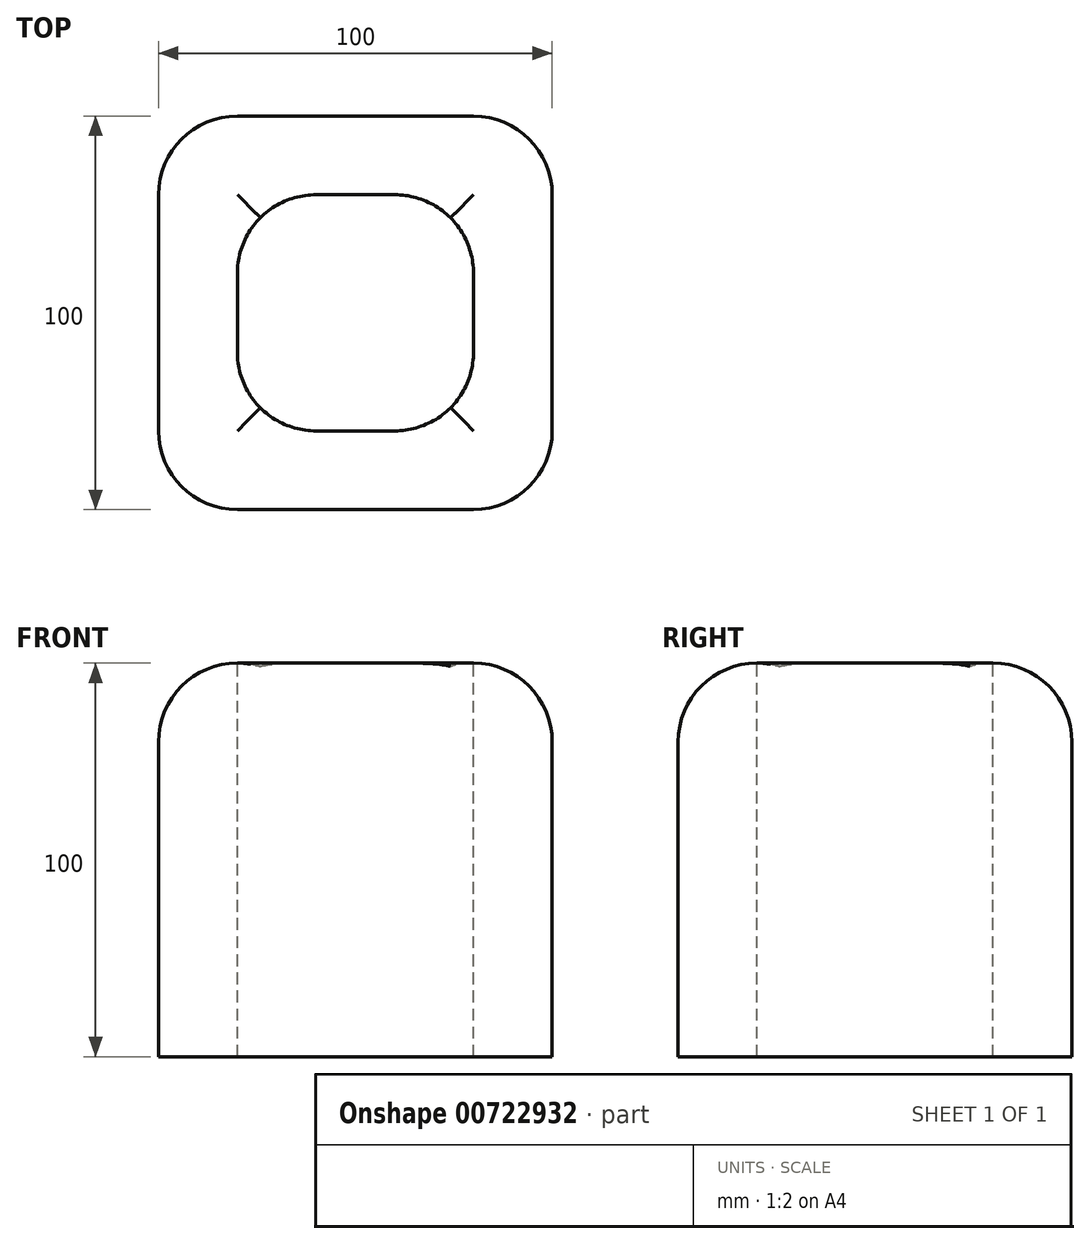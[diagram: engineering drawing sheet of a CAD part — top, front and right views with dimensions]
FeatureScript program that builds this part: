
annotation { "Feature Type Name" : "Feature", "Feature Type Description" : "" }
export const myFeature = defineFeature(function(context is Context, id is Id, definition is map)
    precondition{}
    {
        {
            var Q0;
            Q0=qCreatedBy(makeId("Top.planeOp"),FACE);
            var sketch = newSketch(context, id + "F0", { "sketchPlane" : qUnion([Q0])});
            skLineSegment(sketch, "E0.bottom", {"start": v(-50, 50) * mm, "end": v(50, 50) * mm});
            skLineSegment(sketch, "E0.top", {"start": v(-50, -50) * mm, "end": v(50, -50) * mm});
            skLineSegment(sketch, "E0.left", {"start": v(-50, 50) * mm, "end": v(-50, -50) * mm});
            skLineSegment(sketch, "E0.right", {"start": v(50, 50) * mm, "end": v(50, -50) * mm});
            skSolve(sketch);
        }
        {
            var Q0;
            Q0=makeQuery(id+"F0.imprint","IMPRINT",FACE,{"disambiguationData":[TD([[makeQuery(id+"F0.imprint","IMPRINT",EDGE,{"derivedFrom":sQuery(id+"F0.wireOp",EDGE,"E0.bottom")}),-1.0]])]});
            extrude(context, id + "F1", {"entities" : qUnion([Q0]), "depth" : 100 * mm, "offsetDistance" : 25 * mm});
        }
        {
            var Q0;
            Q0=makeQuery(id+"F1.opExtrude","CAP_EDGE",EDGE,{"disambiguationData":[OSD([sQuery(id+"F0.wireOp",EDGE,"E0.top")])],"isStart":false});
            var Q1;
            Q1=makeQuery(id+"F1.opExtrude","CAP_EDGE",EDGE,{"disambiguationData":[OSD([sQuery(id+"F0.wireOp",EDGE,"E0.right")])],"isStart":false});
            var Q2;
            Q2=makeQuery(id+"F1.opExtrude","CAP_EDGE",EDGE,{"disambiguationData":[OSD([sQuery(id+"F0.wireOp",EDGE,"E0.bottom")])],"isStart":false});
            var Q3;
            Q3=makeQuery(id+"F1.opExtrude","CAP_EDGE",EDGE,{"disambiguationData":[OSD([sQuery(id+"F0.wireOp",EDGE,"E0.left")])],"isStart":false});
            var Q4;
            Q4=makeQuery(id+"F1.opExtrude","SWEPT_EDGE",EDGE,{"disambiguationData":[OSD([sQuery(id+"F0.wireOp",EDGE,"E0.top"),sQuery(id+"F0.wireOp",EDGE,"E0.right")])]});
            var Q5;
            Q5=makeQuery(id+"F1.opExtrude","SWEPT_EDGE",EDGE,{"disambiguationData":[OSD([sQuery(id+"F0.wireOp",EDGE,"E0.top"),sQuery(id+"F0.wireOp",EDGE,"E0.left")])]});
            var Q6;
            Q6=makeQuery(id+"F1.opExtrude","SWEPT_EDGE",EDGE,{"disambiguationData":[OSD([sQuery(id+"F0.wireOp",EDGE,"E0.bottom"),sQuery(id+"F0.wireOp",EDGE,"E0.left")])]});
            var Q7;
            Q7=makeQuery(id+"F1.opExtrude","SWEPT_EDGE",EDGE,{"disambiguationData":[OSD([sQuery(id+"F0.wireOp",EDGE,"E0.bottom"),sQuery(id+"F0.wireOp",EDGE,"E0.right")])]});
            fillet(context, id + "F2", {"entities" : qUnion([Q0, Q1, Q2, Q3, Q4, Q5, Q6, Q7]), "radius" : 20 * mm, "tangentPropagation" : true, "allowEdgeOverflow" : false});
        }
        {
            var Q0;
            Q0=makeQuery(id+"F1.opExtrude","CAP_FACE",FACE,{"disambiguationData":[OSD([sQuery(id+"F0.wireOp",EDGE,"E0.bottom"),sQuery(id+"F0.wireOp",EDGE,"E0.top"),sQuery(id+"F0.wireOp",EDGE,"E0.left"),sQuery(id+"F0.wireOp",EDGE,"E0.right")])],"isStart":false});
            var sketch = newSketch(context, id + "F3", { "sketchPlane" : qUnion([Q0])});
            skLineSegment(sketch, "E1.0.0", {"start": v(-30, -30) * mm, "end": v(30, -30) * mm});
            skLineSegment(sketch, "E1.0.1", {"start": v(30, -30) * mm, "end": v(30, 30) * mm});
            skLineSegment(sketch, "E1.0.2", {"start": v(30, 30) * mm, "end": v(-30, 30) * mm});
            skLineSegment(sketch, "E1.0.3", {"start": v(-30, 30) * mm, "end": v(-30, -30) * mm});
            skSolve(sketch);
        }
        {
            var Q0;
            Q0 = qSketchRegion(id + "F3", true);
            extrude(context, id + "F4", {"entities" : qUnion([Q0]), "operationType" : NewBodyOperationType.REMOVE, "oppositeDirection" : true, "depth" : 138.3 * mm, "offsetDistance" : 25 * mm});
        }
        {
            var Q0;
            Q0=makeQuery(id+"F4.boolean.opBoolean","COPY",EDGE,{"derivedFrom":makeQuery(id+"F4.opExtrude","SWEPT_EDGE",EDGE,{"disambiguationData":[OSD([sQuery(id+"F3.wireOp",EDGE,"E1.0.2"),sQuery(id+"F3.wireOp",EDGE,"E1.0.3")])]})});
            var Q1;
            Q1=makeQuery(id+"F4.boolean.opBoolean","COPY",EDGE,{"derivedFrom":makeQuery(id+"F4.opExtrude","SWEPT_EDGE",EDGE,{"disambiguationData":[OSD([sQuery(id+"F3.wireOp",EDGE,"E1.0.0"),sQuery(id+"F3.wireOp",EDGE,"E1.0.3")])]})});
            var Q2;
            Q2=makeQuery(id+"F4.boolean.opBoolean","COPY",EDGE,{"derivedFrom":makeQuery(id+"F4.opExtrude","SWEPT_EDGE",EDGE,{"disambiguationData":[OSD([sQuery(id+"F3.wireOp",EDGE,"E1.0.0"),sQuery(id+"F3.wireOp",EDGE,"E1.0.1")])]})});
            var Q3;
            Q3=makeQuery(id+"F4.boolean.opBoolean","COPY",EDGE,{"derivedFrom":makeQuery(id+"F4.opExtrude","SWEPT_EDGE",EDGE,{"disambiguationData":[OSD([sQuery(id+"F3.wireOp",EDGE,"E1.0.1"),sQuery(id+"F3.wireOp",EDGE,"E1.0.2")])]})});
            fillet(context, id + "F5", {"entities" : qUnion([Q0, Q1, Q2, Q3]), "radius" : 20 * mm, "tangentPropagation" : true, "allowEdgeOverflow" : false});
        }
    });
